# Revit family: AZURE
name_source: partatom
category: Lighting Fixtures
units: mm (PartAtom-declared; Revit-internal decimal feet)

## family parameters
Always vertical = Yes
Cut with Voids When Loaded = No
Host = Ceiling
Light Source = Yes
Maintain Annotation Orientation = No
OmniClass Number = 23.80.70.11.14.17
OmniClass Title = Direct/Indirect
Part Type = Normal
Room Calculation Point = No
Round Connector Dimension = Use Diameter
Shared = No

## types (1)
- AZR2X2-LED840K050LUNV-xxx
    Apparent Load = 37 VA
    Assembly Code = D5020200
    Color Filter = 16777215
    Default Elevation = 0' - 0"
    Description = LED Configurable Lay-in Backlit Panel Luminaire
    Dimming Lamp Color Temperature Shift = <None>
    Emit Shape Visible in Rendering = No
    Emit from Rectangle Length = 1' - 11 3/4"
    Emit from Rectangle Width = 1' - 11 3/4"
    Height = 0' - 2"
    Housing Finish = Metal - Viscor - White
    Lamp = LED
    Lamp Wattage = 37 VA
    Length = 1' - 11 3/4"
    Lens Finish = Polycarbonate - Viscor - Frosted Round
    Manufacturer = VISIONEERING by VISCOR
    Model = AZURE
    Photometric Web File = AZR2x2-LED-840K050LUNV-G007080.IES
    Tilt Angle = 90.00°
    URL = https://viscor.com
    Voltage = 120 V
    Width = 1' - 11 3/4"

## geometry (parser evidence)
native form markers: Sweep x2
no freeform markers — native parametric forms only
